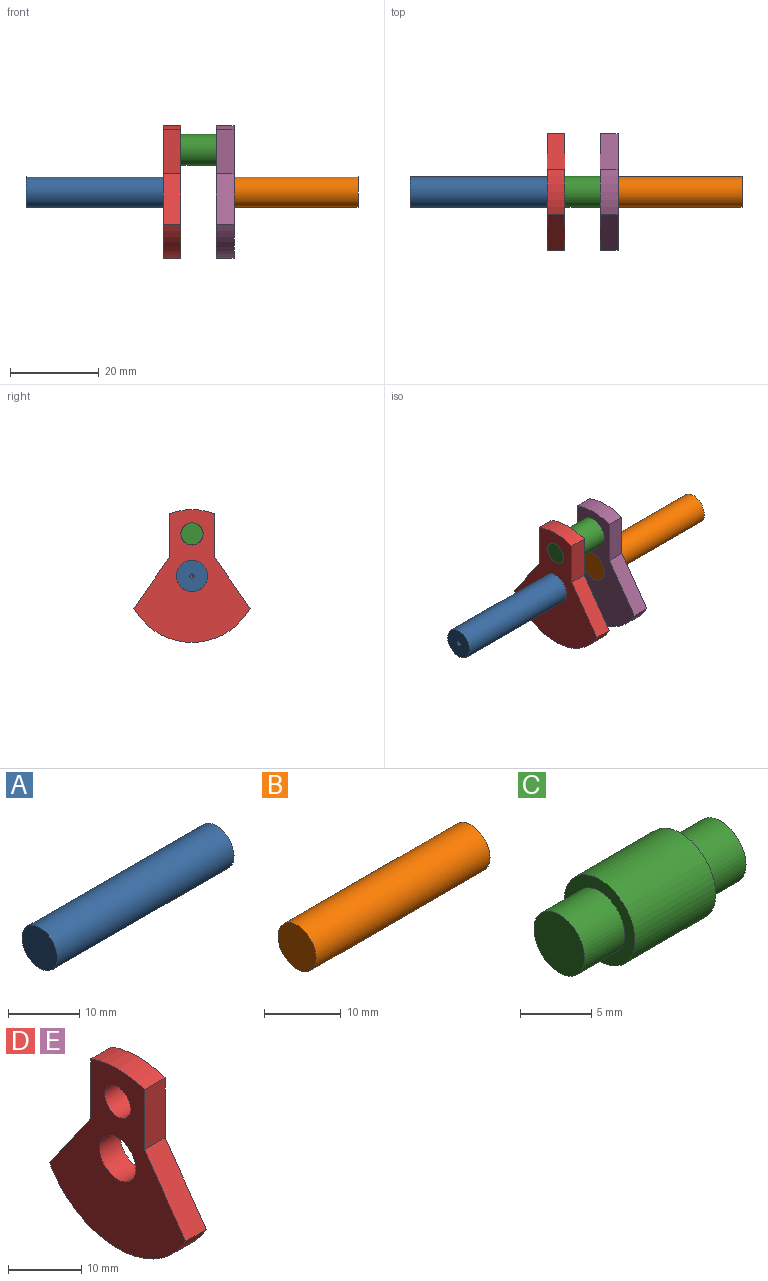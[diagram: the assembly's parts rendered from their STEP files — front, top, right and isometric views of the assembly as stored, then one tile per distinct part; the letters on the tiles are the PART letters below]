
ASSEMBLY  parts=5 mates=4
PART A: 5 faces, bbox 35x7x7 mm
  f0: cylinder r=3.5mm len=35mm, axis (-1,0,0), area 769.7mm2, adj f1,f2
  f1: plane 7x7mm, normal (1,0,0), area 37.7mm2, adj f0,f4
  f2: plane 7x7mm, normal (-1,0,0), area 38.5mm2, adj f0
  f3: cone r=0mm half-angle=59deg, axis (1,0,0), area 0.9mm2, adj f4
  f4: cylinder r=0.5mm len=1mm, axis (1,0,0), area 3.1mm2, adj f1,f3
PART B: 5 faces, bbox 32x7x7 mm
  f0: cylinder r=3.5mm len=32mm, axis (-1,0,0), area 703.7mm2, adj f1,f2
  f1: plane 7x7mm, normal (1,0,0), area 18.8mm2, adj f0,f4
  f2: plane 7x7mm, normal (-1,0,0), area 38.5mm2, adj f0
  f3: cone r=0mm half-angle=59deg, axis (1,0,0), area 22.9mm2, adj f4
  f4: cylinder r=2.5mm len=8mm, axis (1,0,0), area 125.7mm2, adj f1,f3
PART C: 7 faces, bbox 16x7x7 mm
  f0: plane 5x5mm, normal (1,0,0), area 19.6mm2, adj f1
  f1: cylinder r=2.5mm len=5mm, axis (1,0,0), area 62.8mm2, adj f0,f2
  f2: plane 7x7mm, normal (1,0,0), area 18.8mm2, adj f1,f3
  f3: cylinder r=3.5mm len=8mm, axis (1,0,0), area 175.9mm2, adj f2,f4
  f4: plane 7x7mm, normal (-1,0,0), area 18.8mm2, adj f3,f5
  f5: cylinder r=2.5mm len=5mm, axis (1,0,0), area 62.8mm2, adj f4,f6
  f6: plane 5x5mm, normal (-1,0,0), area 19.6mm2, adj f5
PART D: 10 faces, bbox 4x26.3x30 mm
  f0: plane 11.34x7.97mm, normal (0,0.82,0.57), area 55.4mm2, adj f1,f5,f6,f7
  f1: plane 10x4mm, normal (0,1,0), area 40mm2, adj f0,f2,f6,f7
  f2: cylinder r=15mm len=10.32mm, axis (-1,0,0), area 42.1mm2, adj f1,f3,f6,f7
  f3: plane 10x4mm, normal (0,-1,0), area 40mm2, adj f2,f4,f6,f7
  f4: plane 11.34x7.97mm, normal (0,-0.82,0.57), area 55.4mm2, adj f3,f5,f6,f7
  f5: cylinder r=15mm len=26.26mm, axis (-1,0,0), area 127.9mm2, adj f0,f4,f6,f7
  f6: plane 30x26.26mm, normal (1,0,0), area 403.3mm2, adj f0,f1,f2,f3,f4,f5,f8,f9
  f7: plane 30x26.26mm, normal (-1,0,0), area 403.3mm2, adj f0,f1,f2,f3,f4,f5,f8,f9
  f8: cylinder r=3.5mm len=7mm, axis (-1,0,0), area 88mm2, adj f6,f7
  f9: cylinder r=2.5mm len=5mm, axis (-1,0,0), area 62.8mm2, adj f6,f7
PART E: same geometry as D
PLACE A rot(axis=(0,0,1),180deg) t=(2.85,6.21,-10.9)mm
PLACE B t=(10.85,6.21,-10.9)mm
PLACE C t=(6.85,6.21,-1.4)mm
PLACE D t=(-1.15,6.21,-10.9)mm
PLACE E t=(10.85,6.21,-10.9)mm
MATE fastened C.f1 <-> E.f9  axis (1,0,0) through (10.85,6.21,-1.4)mm
MATE fastened C.f1 <-> D.f9  axis (-1,0,0) through (2.85,6.21,-1.4)mm
MATE fastened A.f0 <-> D.f8  axis (1,0,0) through (2.85,6.21,-10.9)mm
MATE fastened E.f8 <-> B.f0  axis (-1,0,0) through (10.85,6.21,-10.9)mm
